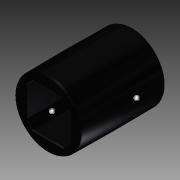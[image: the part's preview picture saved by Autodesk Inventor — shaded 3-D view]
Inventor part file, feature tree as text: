
AUTODESK INVENTOR PART (.ipt)
format: ipt  version: 2015 (Build 190159000, 159)  size: 243,200 bytes
history: native  units: in
note: dims shown in document units (in); Inventor stores cm internally (conversion verified against a paired STEP export)
features: fillet x1, other x1, imported_body x1
ambient origin geometry x8: Origin, YZ Plane, XZ Plane, XY Plane, X Axis, Y Axis, Z Axis, Center Point
bodies: Body1 (feature_tree)
feature tree (3):
  fillet  "Fillet1"  [1 undecoded]
  other  "Spacer HS 1.0 unit"
  imported_body  "Base1"
note: 1 required parameter value undecoded (feature->parameter linkage not recoverable at this tier; creation-order binding heuristic only, values carry confidence <= 0.55)
